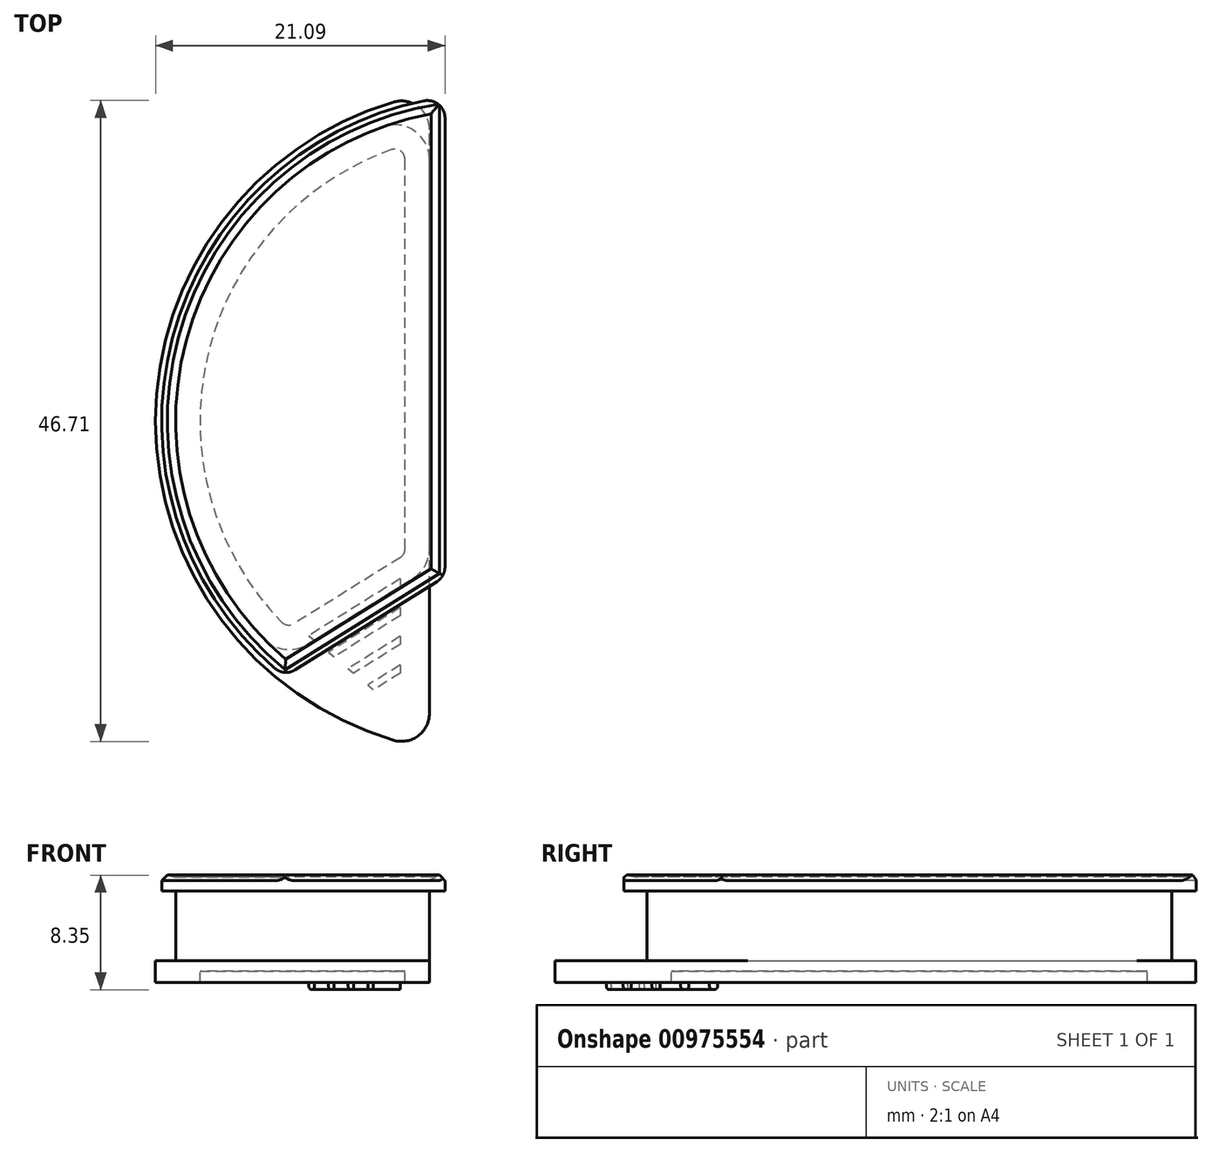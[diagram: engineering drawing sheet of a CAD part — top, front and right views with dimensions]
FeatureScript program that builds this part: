
annotation { "Feature Type Name" : "Feature", "Feature Type Description" : "" }
export const myFeature = defineFeature(function(context is Context, id is Id, definition is map)
    precondition{}
    {
        {
            var Q0;
            Q0=qCreatedBy(makeId("Top.planeOp"),FACE);
            var sketch = newSketch(context, id + "F0", { "sketchPlane" : qUnion([Q0])});
            skCircle(sketch, "E0", {"center": v(0, 0) * mm, "radius": 30.16 * mm});
            skCircle(sketch, "E1", {"center": v(0, 0) * mm, "radius": 28.58 * mm});
            skLineSegment(sketch, "E2.0", {"start": v(-3.17, 28.4) * mm, "end": v(-3.17, -28.4) * mm});
            skLineSegment(sketch, "E3.0", {"start": v(3.17, 28.4) * mm, "end": v(3.17, -28.4) * mm});
            skLineSegment(sketch, "E4", {"start": v(-3.17, -11.33) * mm, "end": v(-14.85, -18.61) * mm});
            skCircle(sketch, "E5", {"center": v(0, 0) * mm, "radius": 23.81 * mm});
            skLineSegment(sketch, "E6.MirrorCS", {"start": v(3.17, -11.33) * mm, "end": v(14.85, -18.61) * mm});
            skSolve(sketch);
        }
        {
            var Q0;
            {var subQ0=sQuery(id+"F0.wireOp",EDGE,"E4");Q0=makeQuery(id+"F0.imprint","IMPRINT",FACE,{"disambiguationData":[TD([[makeQuery(id+"F0.imprint","IMPRINT",EDGE,{"derivedFrom":subQ0}),-1.0]])]});}
            extrude(context, id + "F1", {"entities" : qUnion([Q0]), "depth" : 1.27 * mm, "offsetDistance" : 25.4 * mm});
        }
        {
            var Q0;
            Q0=makeQuery(id+"F1.opExtrude","CAP_FACE",FACE,{"disambiguationData":[OSD([sQuery(id+"F0.wireOp",EDGE,"E2.0"),sQuery(id+"F0.wireOp",EDGE,"E4"),sQuery(id+"F0.wireOp",EDGE,"E5")])],"isStart":false});
            shell(context, id + "F2", {"entities" : qUnion([Q0]), "thickness" : 1.02 * mm});
        }
        {
            var Q0;
            Q0=makeQuery(id+"F1.opExtrude","CAP_FACE",FACE,{"disambiguationData":[OSD([sQuery(id+"F0.wireOp",EDGE,"E2.0"),sQuery(id+"F0.wireOp",EDGE,"E4"),sQuery(id+"F0.wireOp",EDGE,"E5")])],"isStart":true});
            var sketch = newSketch(context, id + "F3", { "sketchPlane" : qUnion([Q0])});
            skLineSegment(sketch, "E7", {"start": v(-14.85, 17.3) * mm, "end": v(-4.3, 10.71) * mm});
            skLineSegment(sketch, "E8", {"start": v(-4.3, 10.71) * mm, "end": v(-4.3, -22.38) * mm});
            skArc(sketch, "E9", {"start": v(-14.85, 17.3) * mm, "mid": v(-22.03, -5.86) * mm, "end": v(-4.3, -22.38) * mm});
            skSolve(sketch);
        }
        {
            var Q0;
            Q0=makeQuery(id+"F3.imprint","IMPRINT",FACE,{"disambiguationData":[TD([[makeQuery(id+"F3.imprint","IMPRINT",EDGE,{"derivedFrom":sQuery(id+"F3.wireOp",EDGE,"E7")}),-1.0]])]});
            extrude(context, id + "F4", {"entities" : qUnion([Q0]), "operationType" : NewBodyOperationType.ADD, "depth" : 5.08 * mm, "offsetDistance" : 25.4 * mm});
        }
        {
            var Q0;
            Q0=makeQuery(id+"F1.opExtrude","CAP_EDGE",EDGE,{"disambiguationData":[OSD([sQuery(id+"F0.wireOp",EDGE,"E5")])],"isStart":false});
            var Q1;
            Q1=makeQuery(id+"F1.opExtrude","CAP_EDGE",EDGE,{"disambiguationData":[OSD([sQuery(id+"F0.wireOp",EDGE,"E2.0")])],"isStart":false});
            var Q2;
            Q2=makeQuery(id+"F1.opExtrude","CAP_EDGE",EDGE,{"disambiguationData":[OSD([sQuery(id+"F0.wireOp",EDGE,"E4")])],"isStart":false});
            chamfer(context, id + "F5", {"entities" : qUnion([Q0, Q1, Q2]), "width" : 0.5 * mm, "tangentPropagation" : true});
        }
        {
            var Q0;
            {var subQ0=sQuery(id+"F0.wireOp",EDGE,"E5");Q0=makeQuery(id+"F2.opShell","OFFSET_EDGE",EDGE,{"disambiguationData":[OSD([subQ0]),TDD([makeQuery(id+"F1.opExtrude","CAP_EDGE",EDGE,{"disambiguationData":[OSD([subQ0])],"isStart":false})])]});}
            var Q1;
            {var subQ0=sQuery(id+"F0.wireOp",EDGE,"E4");Q1=makeQuery(id+"F2.opShell","OFFSET_EDGE",EDGE,{"disambiguationData":[OSD([subQ0]),TDD([makeQuery(id+"F1.opExtrude","CAP_EDGE",EDGE,{"disambiguationData":[OSD([subQ0])],"isStart":false})])]});}
            var Q2;
            {var subQ0=sQuery(id+"F0.wireOp",EDGE,"E2.0");Q2=makeQuery(id+"F2.opShell","OFFSET_EDGE",EDGE,{"disambiguationData":[OSD([subQ0]),TDD([makeQuery(id+"F1.opExtrude","CAP_EDGE",EDGE,{"disambiguationData":[OSD([subQ0])],"isStart":false})])]});}
            fillet(context, id + "F6", {"entities" : qUnion([Q0, Q1, Q2]), "radius" : 5.08 * mm, "tangentPropagation" : true, "allowEdgeOverflow" : false});
        }
        {
            var Q0;
            Q0=makeQuery(id+"F4.opExtrude","CAP_FACE",FACE,{"disambiguationData":[OSD([sQuery(id+"F3.wireOp",EDGE,"E7"),sQuery(id+"F3.wireOp",EDGE,"E8"),sQuery(id+"F3.wireOp",EDGE,"E9")])],"isStart":false});
            var sketch = newSketch(context, id + "F7", { "sketchPlane" : qUnion([Q0])});
            skCircle(sketch, "E10", {"center": v(0, 0) * mm, "radius": 24.26 * mm});
            skLineSegment(sketch, "E11", {"start": v(-4.3, 23.88) * mm, "end": v(-4.3, -23.88) * mm});
            skSolve(sketch);
        }
        {
            var Q0;
            {var subQ4=makeQuery(id+"F4.opExtrude","CAP_EDGE",EDGE,{"disambiguationData":[OSD([sQuery(id+"F3.wireOp",EDGE,"E7")])],"isStart":false});Q0=makeQuery(id+"F7.imprint","IMPRINT",FACE,{"disambiguationData":[TD([[makeQuery(id+"F7.imprint","IMPRINT",EDGE,{"derivedFrom":subQ4}),1.0]])]});}
            var Q1;
            {var subQ1=makeQuery(id+"F4.opExtrude","CAP_EDGE",EDGE,{"disambiguationData":[OSD([sQuery(id+"F3.wireOp",EDGE,"E7")])],"isStart":false});Q1=makeQuery(id+"F7.imprint","IMPRINT",FACE,{"disambiguationData":[TD([[makeQuery(id+"F7.imprint","IMPRINT",EDGE,{"derivedFrom":subQ1}),-1.0]])]});}
            extrude(context, id + "F8", {"entities" : qUnion([Q0, Q1]), "operationType" : NewBodyOperationType.ADD, "depth" : 1.59 * mm, "offsetDistance" : 25.4 * mm});
        }
        {
            var Q0;
            Q0=makeQuery(id+"F1.opExtrude","SWEPT_EDGE",EDGE,{"disambiguationData":[OSD([sQuery(id+"F0.wireOp",EDGE,"E2.0"),sQuery(id+"F0.wireOp",EDGE,"E4")])]});
            var Q1;
            Q1=makeQuery(id+"F1.opExtrude","SWEPT_EDGE",EDGE,{"disambiguationData":[OSD([sQuery(id+"F0.wireOp",EDGE,"E4"),sQuery(id+"F0.wireOp",EDGE,"E5")])]});
            var Q2;
            Q2=makeQuery(id+"F1.opExtrude","SWEPT_EDGE",EDGE,{"disambiguationData":[OSD([sQuery(id+"F0.wireOp",EDGE,"E2.0"),sQuery(id+"F0.wireOp",EDGE,"E5")])]});
            fillet(context, id + "F9", {"entities" : qUnion([Q0, Q1, Q2]), "radius" : 1.27 * mm, "tangentPropagation" : true, "allowEdgeOverflow" : false});
        }
        {
            var Q0;
            Q0=makeQuery(id+"F4.opExtrude","SWEPT_EDGE",EDGE,{"disambiguationData":[OSD([sQuery(id+"F3.wireOp",EDGE,"E7"),sQuery(id+"F3.wireOp",EDGE,"E8")])]});
            var Q1;
            Q1=makeQuery(id+"F4.opExtrude","SWEPT_EDGE",EDGE,{"disambiguationData":[OSD([sQuery(id+"F3.wireOp",EDGE,"E7"),sQuery(id+"F3.wireOp",EDGE,"E9")])]});
            var Q2;
            {var subQ0=sQuery(id+"F3.wireOp",EDGE,"E9");var subQ1=sQuery(id+"F3.wireOp",EDGE,"E8");Q2=makeQuery(id+"F8.boolean.opBoolean","MERGE",EDGE,{"derivedFrom":[makeQuery(id+"F4.opExtrude","SWEPT_EDGE",EDGE,{"disambiguationData":[OSD([subQ1,subQ0])]}),makeQuery(id+"F8.opExtrude","SWEPT_EDGE",EDGE,{"disambiguationData":[OSD([subQ1,subQ0])]})]});}
            fillet(context, id + "F10", {"entities" : qUnion([Q0, Q1, Q2]), "radius" : 2.54 * mm, "tangentPropagation" : true, "allowEdgeOverflow" : false});
        }
        {
            var Q0;
            {var subQ0=sQuery(id+"F7.wireOp",EDGE,"E11");var subQ1=sQuery(id+"F7.wireOp",EDGE,"E10");Q0=makeQuery(id+"F8.opExtrude","SWEPT_EDGE",EDGE,{"disambiguationData":[OSD([subQ1,subQ0]),TDD([makeQuery(id+"F7.imprint","INTERSECT",VERTEX,{"disambiguationData":[OD(1.0)],"derivedFrom":[subQ1,subQ0]})])]});}
            var Q1;
            {var subQ0=sQuery(id+"F7.wireOp",EDGE,"E11");var subQ1=sQuery(id+"F7.wireOp",EDGE,"E10");Q1=makeQuery(id+"F8.opExtrude","SWEPT_EDGE",EDGE,{"disambiguationData":[OSD([subQ1,subQ0]),TDD([makeQuery(id+"F7.imprint","INTERSECT",VERTEX,{"disambiguationData":[OD(0.0)],"derivedFrom":[subQ1,subQ0]})])]});}
            fillet(context, id + "F11", {"entities" : qUnion([Q0, Q1]), "radius" : 2.03 * mm, "tangentPropagation" : true, "allowEdgeOverflow" : false});
        }
        {
            var Q0;
            Q0=makeQuery(id+"F8.opExtrude","CAP_FACE",FACE,{"disambiguationData":[OSD([sQuery(id+"F7.wireOp",EDGE,"E10"),sQuery(id+"F7.wireOp",EDGE,"E11")])],"isStart":false});
            shell(context, id + "F12", {"entities" : qUnion([Q0]), "thickness" : 1.78 * mm});
        }
        {
            var Q0;
            Q0=makeQuery(id+"F12.opShell","OFFSET_FACE",FACE,{"disambiguationData":[OSD([sQuery(id+"F0.wireOp",EDGE,"E2.0"),sQuery(id+"F0.wireOp",EDGE,"E4"),sQuery(id+"F0.wireOp",EDGE,"E5")])]});
            extrude(context, id + "F13", {"entities" : qUnion([Q0]), "operationType" : NewBodyOperationType.ADD, "depth" : 5.08 * mm, "offsetDistance" : 25.4 * mm});
        }
        {
            var Q0;
            Q0=makeQuery(id+"F8.opExtrude","CAP_FACE",FACE,{"disambiguationData":[OSD([sQuery(id+"F7.wireOp",EDGE,"E10"),sQuery(id+"F7.wireOp",EDGE,"E11")])],"isStart":false});
            var sketch = newSketch(context, id + "F14", { "sketchPlane" : qUnion([Q0])});
            skLineSegment(sketch, "E12", {"start": v(-6.45, 11.48) * mm, "end": v(-13.1, 15.63) * mm});
            skLineSegment(sketch, "E13.0", {"start": v(-6.45, 13.58) * mm, "end": v(-11.66, 16.83) * mm});
            skLineSegment(sketch, "E14.0", {"start": v(-6.45, 15.68) * mm, "end": v(-10.23, 18.04) * mm});
            skLineSegment(sketch, "E15.0", {"start": v(-6.45, 17.77) * mm, "end": v(-8.8, 19.24) * mm});
            skLineSegment(sketch, "E16", {"start": v(-6.45, 9.3) * mm, "end": v(-6.45, 19.55) * mm});
            skLineSegment(sketch, "E17", {"start": v(-14.14, 14.75) * mm, "end": v(-6.34, 21.3) * mm});
            skLineSegment(sketch, "E18.0", {"start": v(-6.45, 12.08) * mm, "end": v(-12.68, 15.97) * mm});
            skLineSegment(sketch, "E19.0", {"start": v(-6.45, 14.18) * mm, "end": v(-11.25, 17.18) * mm});
            skLineSegment(sketch, "E20.0", {"start": v(-6.45, 16.27) * mm, "end": v(-9.82, 18.38) * mm});
            skLineSegment(sketch, "E21.0", {"start": v(-6.45, 18.37) * mm, "end": v(-8.4, 19.58) * mm});
            skSolve(sketch);
        }
        {
            var Q0;
            {var subQ0=sQuery(id+"F14.wireOp",EDGE,"E12");Q0=makeQuery(id+"F14.imprint","IMPRINT",FACE,{"disambiguationData":[TD([[makeQuery(id+"F14.imprint","IMPRINT",EDGE,{"derivedFrom":subQ0}),-1.0]])]});}
            var Q1;
            {var subQ0=sQuery(id+"F14.wireOp",EDGE,"E13.0");Q1=makeQuery(id+"F14.imprint","IMPRINT",FACE,{"disambiguationData":[TD([[makeQuery(id+"F14.imprint","IMPRINT",EDGE,{"derivedFrom":subQ0}),-1.0]])]});}
            var Q2;
            {var subQ0=sQuery(id+"F14.wireOp",EDGE,"E14.0");Q2=makeQuery(id+"F14.imprint","IMPRINT",FACE,{"disambiguationData":[TD([[makeQuery(id+"F14.imprint","IMPRINT",EDGE,{"derivedFrom":subQ0}),-1.0]])]});}
            var Q3;
            {var subQ0=sQuery(id+"F14.wireOp",EDGE,"E15.0");Q3=makeQuery(id+"F14.imprint","IMPRINT",FACE,{"disambiguationData":[TD([[makeQuery(id+"F14.imprint","IMPRINT",EDGE,{"derivedFrom":subQ0}),-1.0]])]});}
            extrude(context, id + "F15", {"entities" : qUnion([Q0, Q1, Q2, Q3]), "operationType" : NewBodyOperationType.ADD, "depth" : 0.5 * mm, "offsetDistance" : 25.4 * mm});
        }
        {
            var Q0;
            Q0=makeQuery(id+"F15.opExtrude","CAP_EDGE",EDGE,{"disambiguationData":[OSD([sQuery(id+"F14.wireOp",EDGE,"E18.0")])],"isStart":false});
            var Q1;
            Q1=makeQuery(id+"F15.opExtrude","CAP_EDGE",EDGE,{"disambiguationData":[OSD([sQuery(id+"F14.wireOp",EDGE,"E12")])],"isStart":false});
            var Q2;
            Q2=makeQuery(id+"F15.opExtrude","CAP_EDGE",EDGE,{"disambiguationData":[OSD([sQuery(id+"F14.wireOp",EDGE,"E13.0")])],"isStart":false});
            var Q3;
            Q3=makeQuery(id+"F15.opExtrude","CAP_EDGE",EDGE,{"disambiguationData":[OSD([sQuery(id+"F14.wireOp",EDGE,"E19.0")])],"isStart":false});
            var Q4;
            Q4=makeQuery(id+"F15.opExtrude","CAP_EDGE",EDGE,{"disambiguationData":[OSD([sQuery(id+"F14.wireOp",EDGE,"E14.0")])],"isStart":false});
            var Q5;
            Q5=makeQuery(id+"F15.opExtrude","CAP_EDGE",EDGE,{"disambiguationData":[OSD([sQuery(id+"F14.wireOp",EDGE,"E20.0")])],"isStart":false});
            var Q6;
            Q6=makeQuery(id+"F15.opExtrude","CAP_EDGE",EDGE,{"disambiguationData":[OSD([sQuery(id+"F14.wireOp",EDGE,"E21.0")])],"isStart":false});
            var Q7;
            Q7=makeQuery(id+"F15.opExtrude","CAP_EDGE",EDGE,{"disambiguationData":[OSD([sQuery(id+"F14.wireOp",EDGE,"E15.0")])],"isStart":false});
            fillet(context, id + "F16", {"entities" : qUnion([Q0, Q1, Q2, Q3, Q4, Q5, Q6, Q7]), "radius" : 0.25 * mm, "tangentPropagation" : true, "allowEdgeOverflow" : false});
        }
    });
